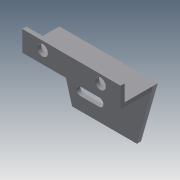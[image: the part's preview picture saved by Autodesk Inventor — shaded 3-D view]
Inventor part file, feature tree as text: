
AUTODESK INVENTOR PART (.ipt)
format: ipt  version: 2013 (Build 170138000, 138)  size: 187,904 bytes
history: native  units: mm
features: extrude x11, sketch x11
ambient origin geometry x8: Origin, YZ Plane, XZ Plane, XY Plane, X Axis, Y Axis, Z Axis, Center Point
bodies: Solid1 (feature_tree)
feature tree (22):
  extrude  "Extrusion1"  Depth=12.1mm
  extrude  "Extrusion2"  Depth=1.5mm
  extrude  "Extrusion3"  Depth=1.5mm TaperAngle=0.0deg
  extrude  "Extrusion4"  Depth=6.0mm TaperAngle=0.0deg
  extrude  "Extrusion5"  Depth=3.5mm
  extrude  "Extrusion6"  Depth=3.0mm
  extrude  "Extrusion7"  Depth=2.0mm TaperAngle=0.0deg
  extrude  "Extrusion8"  Depth=9.0mm
  extrude  "Extrusion9"  Depth=4.0mm
  extrude  "Extrusion10"  Depth=3.0mm
  extrude  "Extrusion11"  Depth=21.186mm
  sketch  "Sketch1"  dims[d0=36.0mm d1=12.1mm]
  sketch  "Sketch2"  dims[d2=1.5mm d3=0.0mm d4=1.5mm]
  sketch  "Sketch3"  dims[d5=30.0mm d6=0.0mm d7=1.5mm d8=0.0mm]
  sketch  "Sketch4"  dims[d9=1.5mm d10=6.0mm d11=0.0mm]
  sketch  "Sketch5"  dims[d12=5.0mm d13=3.5mm]
  sketch  "Sketch6"  dims[d14=3.5mm d15=3.0mm]
  sketch  "Sketch7"  dims[d16=3.0mm d17=2.0mm d18=0.0mm]
  sketch  "Sketch8"  dims[d19=9.0mm d20=9.0mm]
  sketch  "Sketch9"  dims[d21=2.0mm d22=0.0mm d23=4.0mm]
  sketch  "Sketch10"  dims[d25=3.0mm d26=3.0mm]
  sketch  "Sketch11"  dims[d27=2.0mm d28=0.0mm d29=21.186mm d30=4.0mm d31=4.0mm d32=1.5mm d33=0.0mm d34=1.5mm d35=0.0mm d36=10.0mm d37=1.5mm d38=0.0mm d39=5.4mm d40=6.3mm d41=3.5mm d42=7.0mm d43=3.0mm d44=3.0mm d45=1.5mm d46=0.0mm]
